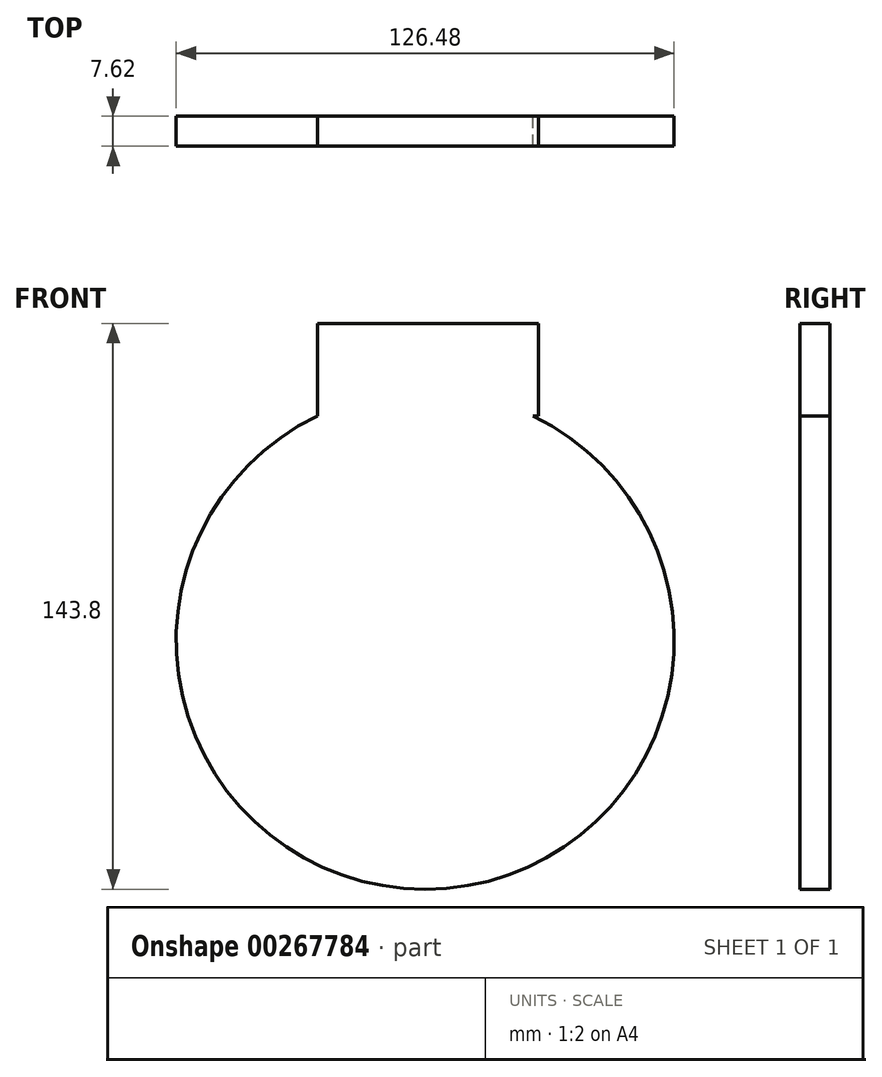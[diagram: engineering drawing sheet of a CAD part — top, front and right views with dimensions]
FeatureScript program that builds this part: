
annotation { "Feature Type Name" : "Feature", "Feature Type Description" : "" }
export const myFeature = defineFeature(function(context is Context, id is Id, definition is map)
    precondition{}
    {
        {
            var Q0;
            Q0=qCreatedBy(makeId("Front.planeOp"),FACE);
            var sketch = newSketch(context, id + "F0", { "sketchPlane" : qUnion([Q0])});
            skCircle(sketch, "E0", {"center": v(0, 0) * mm, "radius": 63.24 * mm});
            skLineSegment(sketch, "E1.bottom", {"start": v(-27.4, 57) * mm, "end": v(28.85, 57) * mm});
            skLineSegment(sketch, "E1.top", {"start": v(-27.4, 80.56) * mm, "end": v(28.85, 80.56) * mm});
            skLineSegment(sketch, "E1.left", {"start": v(-27.4, 57) * mm, "end": v(-27.4, 80.56) * mm});
            skLineSegment(sketch, "E1.right", {"start": v(28.85, 57) * mm, "end": v(28.85, 80.56) * mm});
            skSolve(sketch);
        }
        {
            var Q0;
            Q0=makeQuery(id+"F0.imprint","IMPRINT",FACE,{"disambiguationData":[TD([[makeQuery(id+"F0.imprint","IMPRINT",EDGE,{"derivedFrom":sQuery(id+"F0.wireOp",EDGE,"E0")}),1.0]])]});
            extrude(context, id + "F1", {"entities" : qUnion([Q0]), "depth" : 7.62 * mm});
        }
        {
            var Q0;
            Q0 = qSketchRegion(id + "F0", true);
            extrude(context, id + "F2", {"entities" : qUnion([Q0]), "operationType" : NewBodyOperationType.ADD, "depth" : 7.62 * mm});
        }
    });
